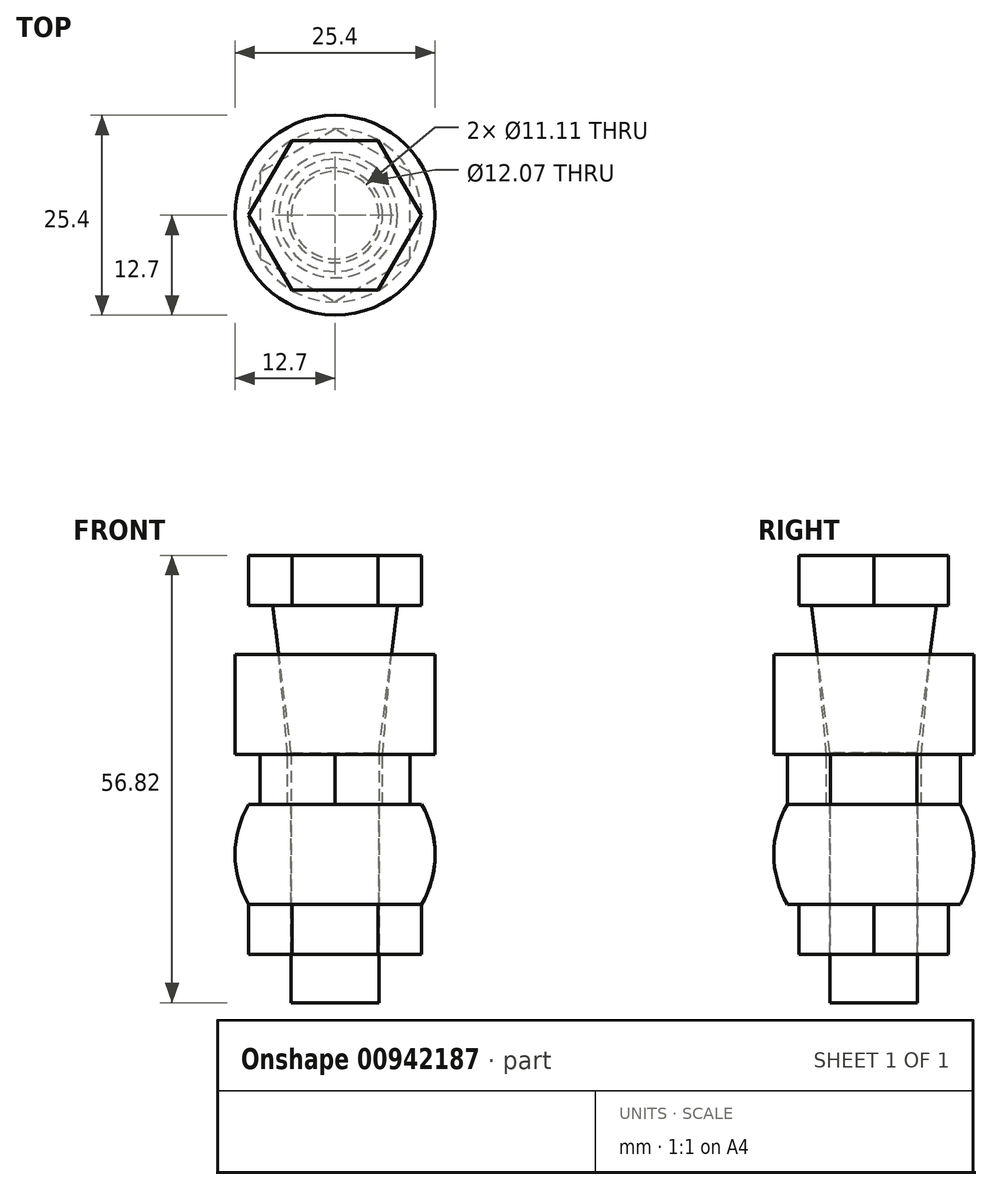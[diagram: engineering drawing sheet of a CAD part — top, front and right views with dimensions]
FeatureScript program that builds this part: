
annotation { "Feature Type Name" : "Feature", "Feature Type Description" : "" }
export const myFeature = defineFeature(function(context is Context, id is Id, definition is map)
    precondition{}
    {
        {
            var Q0;
            Q0=qCreatedBy(makeId("Front.planeOp"),FACE);
            var sketch = newSketch(context, id + "F0", { "sketchPlane" : qUnion([Q0])});
            skLineSegment(sketch, "E0", {"start": v(0, 9.3) * mm, "end": v(0, -9.3) * mm, "construction": true});
            skLineSegment(sketch, "E1", {"start": v(-7.14, 6.35) * mm, "end": v(-12.7, 6.35) * mm});
            skLineSegment(sketch, "E2", {"start": v(-12.7, 6.35) * mm, "end": v(-12.7, -6.35) * mm});
            skLineSegment(sketch, "E3", {"start": v(-12.7, -6.35) * mm, "end": v(-6.03, -6.35) * mm});
            skLineSegment(sketch, "E4", {"start": v(-6.03, -6.35) * mm, "end": v(-7.14, 6.35) * mm});
            skSolve(sketch);
        }
        {
            var Q0;
            Q0=makeQuery(id+"F0.imprint","IMPRINT",FACE,{"disambiguationData":[TD([[makeQuery(id+"F0.imprint","IMPRINT",EDGE,{"derivedFrom":sQuery(id+"F0.wireOp",EDGE,"E1")}),1.0]])]});
            var Q1;
            Q1=sQuery(id+"F0.wireOp",EDGE,"E0");
            revolve(context, id + "F1", {"surfaceOperationType" : NewSurfaceOperationType.NEW, "entities" : qUnion([Q0]), "axis" : qUnion([Q1]), "revolveType" : RevolveType.FULL});
        }
        {
            var Q0;
            Q0=qCreatedBy(makeId("Front.planeOp"),FACE);
            var sketch = newSketch(context, id + "F2", { "sketchPlane" : qUnion([Q0])});
            skLineSegment(sketch, "E5", {"start": v(-7.94, 12.59) * mm, "end": v(-5.56, -6.13) * mm});
            skLineSegment(sketch, "E6", {"start": v(-5.56, -6.13) * mm, "end": v(-5.56, -37.88) * mm});
            skLineSegment(sketch, "E7", {"start": v(-5.56, -37.88) * mm, "end": v(0, -37.88) * mm});
            skLineSegment(sketch, "E8", {"start": v(0, -37.88) * mm, "end": v(0, 12.59) * mm});
            skLineSegment(sketch, "E9", {"start": v(-7.94, 12.59) * mm, "end": v(0, 12.59) * mm});
            skSolve(sketch);
        }
        {
            var Q0;
            Q0=makeQuery(id+"F2.imprint","IMPRINT",FACE,{"disambiguationData":[TD([[makeQuery(id+"F2.imprint","IMPRINT",EDGE,{"derivedFrom":sQuery(id+"F2.wireOp",EDGE,"E5")}),1.0]])]});
            var Q1;
            Q1=sQuery(id+"F2.wireOp",EDGE,"E8");
            revolve(context, id + "F3", {"surfaceOperationType" : NewSurfaceOperationType.NEW, "entities" : qUnion([Q0]), "axis" : qUnion([Q1]), "revolveType" : RevolveType.FULL});
        }
        {
            var Q0;
            Q0=makeQuery(id+"F3.opRevolve","SWEPT_FACE",FACE,{"disambiguationData":[OSD([sQuery(id+"F2.wireOp",EDGE,"E9")])]});
            var sketch = newSketch(context, id + "F4", { "sketchPlane" : qUnion([Q0])});
            skCircle(sketch, "E10.cCircle", {"center": v(0, 0) * mm, "radius": 9.5 * mm, "construction": true});
            skLineSegment(sketch, "E10.0", {"start": v(5.48, 9.5) * mm, "end": v(10.97, 0) * mm});
            skLineSegment(sketch, "E10.1", {"start": v(10.97, 0) * mm, "end": v(5.48, -9.5) * mm});
            skLineSegment(sketch, "E10.2", {"start": v(5.48, -9.5) * mm, "end": v(-5.48, -9.5) * mm});
            skLineSegment(sketch, "E10.3", {"start": v(-5.48, -9.5) * mm, "end": v(-10.97, 0) * mm});
            skLineSegment(sketch, "E10.4", {"start": v(-10.97, 0) * mm, "end": v(-5.48, 9.5) * mm});
            skLineSegment(sketch, "E10.5", {"start": v(-5.48, 9.5) * mm, "end": v(5.48, 9.5) * mm});
            skPoint(sketch, "E10.0.midPoint", {"position": v(8.23, 4.75) * mm});
            skSolve(sketch);
        }
        {
            var Q0;
            Q0=makeQuery(id+"F4.imprint","IMPRINT",FACE,{"disambiguationData":[TD([[makeQuery(id+"F4.imprint","IMPRINT",EDGE,{"derivedFrom":sQuery(id+"F4.wireOp",EDGE,"E10.0")}),-1.0]])]});
            var Q1;
            Q1=makeQuery(id+"F4.imprint","IMPRINT",FACE,{"disambiguationData":[TD([[makeQuery(id+"F4.imprint","IMPRINT",EDGE,{"derivedFrom":makeQuery(id+"F3.opRevolve","SWEPT_EDGE",EDGE,{"disambiguationData":[OSD([sQuery(id+"F2.wireOp",EDGE,"E5"),sQuery(id+"F2.wireOp",EDGE,"E9")])]})}),-1.0]])]});
            extrude(context, id + "F5", {"entities" : qUnion([Q0, Q1]), "operationType" : NewBodyOperationType.ADD, "depth" : 6.35 * mm, "offsetDistance" : 25.4 * mm});
        }
        {
            var Q0;
            Q0=qCreatedBy(makeId("Front.planeOp"),FACE);
            var sketch = newSketch(context, id + "F6", { "sketchPlane" : qUnion([Q0])});
            skLineSegment(sketch, "E11", {"start": v(-5.56, -12.7) * mm, "end": v(-5.56, -25.4) * mm});
            skLineSegment(sketch, "E12", {"start": v(-5.56, -25.4) * mm, "end": v(-11, -25.4) * mm});
            skLineSegment(sketch, "E13", {"start": v(-5.56, -12.7) * mm, "end": v(-11, -12.7) * mm});
            skArc(sketch, "E14", {"start": v(-11, -12.7) * mm, "mid": v(-12.7, -19.05) * mm, "end": v(-11, -25.4) * mm});
            skLineSegment(sketch, "E15.0", {"start": v(0, 9.3) * mm, "end": v(0, -9.3) * mm, "construction": true});
            skSolve(sketch);
        }
        {
            var Q0;
            Q0=makeQuery(id+"F6.imprint","IMPRINT",FACE,{"disambiguationData":[TD([[makeQuery(id+"F6.imprint","IMPRINT",EDGE,{"derivedFrom":sQuery(id+"F6.wireOp",EDGE,"E11")}),-1.0]])]});
            var Q1;
            Q1=sQuery(id+"F6.wireOp",EDGE,"E15.0");
            revolve(context, id + "F7", {"surfaceOperationType" : NewSurfaceOperationType.NEW, "entities" : qUnion([Q0]), "axis" : qUnion([Q1]), "revolveType" : RevolveType.FULL});
        }
        {
            var Q0;
            Q0=makeQuery(id+"F1.opRevolve","SWEPT_FACE",FACE,{"disambiguationData":[OSD([sQuery(id+"F0.wireOp",EDGE,"E3")])]});
            var sketch = newSketch(context, id + "F8", { "sketchPlane" : qUnion([Q0])});
            skCircle(sketch, "E16.cCircle", {"center": v(0, 0) * mm, "radius": 9.5 * mm, "construction": true});
            skLineSegment(sketch, "E16.0", {"start": v(0, 10.97) * mm, "end": v(9.5, 5.48) * mm});
            skLineSegment(sketch, "E16.1", {"start": v(9.5, 5.48) * mm, "end": v(9.5, -5.48) * mm});
            skLineSegment(sketch, "E16.2", {"start": v(9.5, -5.48) * mm, "end": v(0, -10.97) * mm});
            skLineSegment(sketch, "E16.3", {"start": v(0, -10.97) * mm, "end": v(-9.5, -5.48) * mm});
            skLineSegment(sketch, "E16.4", {"start": v(-9.5, -5.48) * mm, "end": v(-9.5, 5.48) * mm});
            skLineSegment(sketch, "E16.5", {"start": v(-9.5, 5.48) * mm, "end": v(0, 10.97) * mm});
            skPoint(sketch, "E16.0.midPoint", {"position": v(4.75, 8.23) * mm});
            skSolve(sketch);
        }
        {
            var Q0;
            Q0=makeQuery(id+"F8.imprint","IMPRINT",FACE,{"disambiguationData":[TD([[makeQuery(id+"F8.imprint","IMPRINT",EDGE,{"derivedFrom":sQuery(id+"F8.wireOp",EDGE,"E16.0")}),-1.0]])]});
            extrude(context, id + "F9", {"entities" : qUnion([Q0]), "depth" : 6.35 * mm, "offsetDistance" : 25.4 * mm});
        }
        {
            var Q0;
            Q0=makeQuery(id+"F7.opRevolve","SWEPT_FACE",FACE,{"disambiguationData":[OSD([sQuery(id+"F6.wireOp",EDGE,"E12")])]});
            var sketch = newSketch(context, id + "F10", { "sketchPlane" : qUnion([Q0])});
            skLineSegment(sketch, "E17.0", {"start": v(-5.48, 9.5) * mm, "end": v(-10.97, 0) * mm});
            skLineSegment(sketch, "E18.0", {"start": v(5.48, 9.5) * mm, "end": v(-5.48, 9.5) * mm});
            skLineSegment(sketch, "E19.0", {"start": v(10.97, 0) * mm, "end": v(5.48, 9.5) * mm});
            skLineSegment(sketch, "E20.0", {"start": v(5.48, -9.5) * mm, "end": v(10.97, 0) * mm});
            skLineSegment(sketch, "E21.0", {"start": v(-5.48, -9.5) * mm, "end": v(5.48, -9.5) * mm});
            skLineSegment(sketch, "E22.0", {"start": v(-10.97, 0) * mm, "end": v(-5.48, -9.5) * mm});
            skCircle(sketch, "E23.0", {"center": v(0, 0) * mm, "radius": 5.56 * mm});
            skSolve(sketch);
        }
        {
            var Q0;
            Q0=makeQuery(id+"F10.imprint","IMPRINT",FACE,{"disambiguationData":[TD([[makeQuery(id+"F10.imprint","IMPRINT",EDGE,{"derivedFrom":sQuery(id+"F10.wireOp",EDGE,"E17.0")}),1.0]])]});
            extrude(context, id + "F11", {"entities" : qUnion([Q0]), "depth" : 6.35 * mm, "offsetDistance" : 25.4 * mm});
        }
    });
